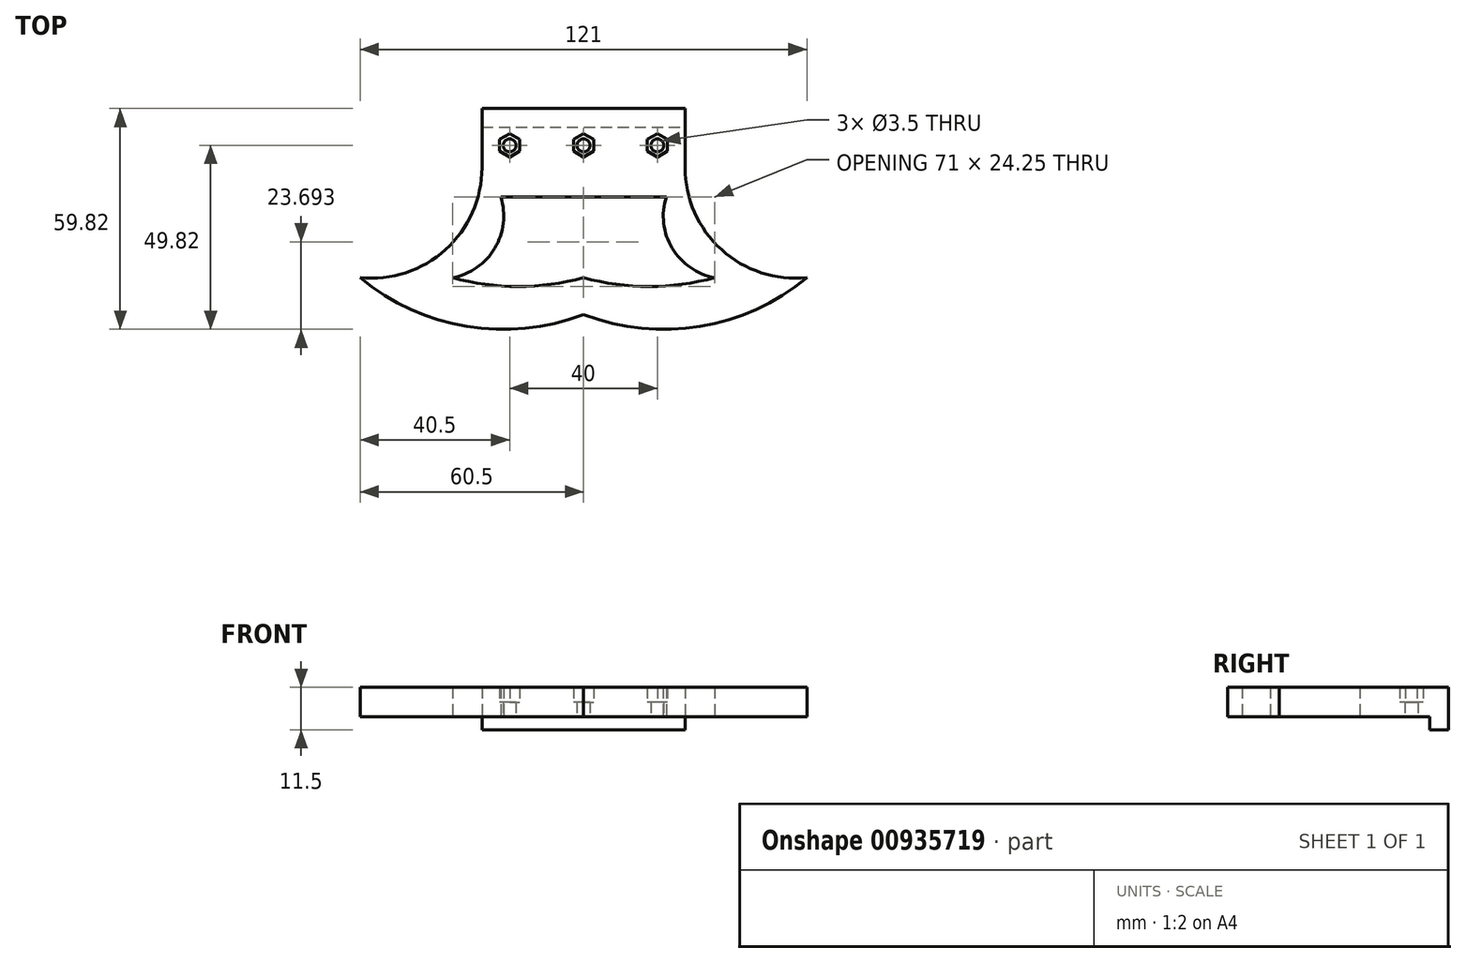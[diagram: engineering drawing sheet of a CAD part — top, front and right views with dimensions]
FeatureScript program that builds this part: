
annotation { "Feature Type Name" : "Feature", "Feature Type Description" : "" }
export const myFeature = defineFeature(function(context is Context, id is Id, definition is map)
    precondition{}
    {
        {
            var Q0;
            Q0=qCreatedBy(makeId("Top.planeOp"),FACE);
            var sketch = newSketch(context, id + "F0", { "sketchPlane" : qUnion([Q0])});
            skLineSegment(sketch, "E0.bottom", {"start": v(-27.5, -8) * mm, "end": v(27.5, -8) * mm});
            skLineSegment(sketch, "E0.top", {"start": v(-27.5, 8) * mm, "end": v(27.5, 8) * mm});
            skLineSegment(sketch, "E0.left", {"start": v(-27.5, -8) * mm, "end": v(-27.5, 8) * mm});
            skLineSegment(sketch, "E0.right", {"start": v(27.5, -8) * mm, "end": v(27.5, 8) * mm});
            skPoint(sketch, "E0.middle", {"position": v(0, 0) * mm});
            skLineSegment(sketch, "E1", {"start": v(-27.5, 3) * mm, "end": v(27.5, 3) * mm});
            skCircle(sketch, "E2.cCircle", {"center": v(0, -2) * mm, "radius": 2.75 * mm, "construction": true});
            skLineSegment(sketch, "E2.0", {"start": v(-2.75, -3.59) * mm, "end": v(-2.75, -0.41) * mm});
            skLineSegment(sketch, "E2.1", {"start": v(-2.75, -0.41) * mm, "end": v(0, 1.18) * mm});
            skLineSegment(sketch, "E2.2", {"start": v(0, 1.18) * mm, "end": v(2.75, -0.41) * mm});
            skLineSegment(sketch, "E2.3", {"start": v(2.75, -0.41) * mm, "end": v(2.75, -3.59) * mm});
            skLineSegment(sketch, "E2.4", {"start": v(2.75, -3.59) * mm, "end": v(0, -5.18) * mm});
            skLineSegment(sketch, "E2.5", {"start": v(0, -5.18) * mm, "end": v(-2.75, -3.59) * mm});
            skPoint(sketch, "E2.0.midPoint", {"position": v(-2.75, -2) * mm});
            skCircle(sketch, "E3", {"center": v(0, -2) * mm, "radius": 1.75 * mm});
            skCircle(sketch, "E4.cCircle", {"center": v(-20, -2) * mm, "radius": 2.75 * mm, "construction": true});
            skLineSegment(sketch, "E4.0", {"start": v(-17.25, -0.41) * mm, "end": v(-17.25, -3.59) * mm});
            skLineSegment(sketch, "E4.1", {"start": v(-17.25, -3.59) * mm, "end": v(-20, -5.18) * mm});
            skLineSegment(sketch, "E4.2", {"start": v(-20, -5.18) * mm, "end": v(-22.75, -3.59) * mm});
            skLineSegment(sketch, "E4.3", {"start": v(-22.75, -3.59) * mm, "end": v(-22.75, -0.41) * mm});
            skLineSegment(sketch, "E4.4", {"start": v(-22.75, -0.41) * mm, "end": v(-20, 1.18) * mm});
            skLineSegment(sketch, "E4.5", {"start": v(-20, 1.18) * mm, "end": v(-17.25, -0.41) * mm});
            skPoint(sketch, "E4.0.midPoint", {"position": v(-17.25, -2) * mm});
            skCircle(sketch, "E5", {"center": v(-20, -2) * mm, "radius": 1.75 * mm});
            skLineSegment(sketch, "E6.MirrorCS", {"start": v(17.25, -0.41) * mm, "end": v(17.25, -3.59) * mm});
            skLineSegment(sketch, "E7.MirrorCS", {"start": v(17.25, -3.59) * mm, "end": v(20, -5.18) * mm});
            skLineSegment(sketch, "E8.MirrorCS", {"start": v(20, -5.18) * mm, "end": v(22.75, -3.59) * mm});
            skLineSegment(sketch, "E9.MirrorCS", {"start": v(22.75, -3.59) * mm, "end": v(22.75, -0.41) * mm});
            skCircle(sketch, "E10.MirrorC", {"center": v(20, -2) * mm, "radius": 1.75 * mm});
            skCircle(sketch, "E11.MirrorC", {"center": v(20, -2) * mm, "radius": 2.75 * mm, "construction": true});
            skPoint(sketch, "E12.MirrorP", {"position": v(17.25, -2) * mm});
            skLineSegment(sketch, "E13.MirrorCS", {"start": v(20, 1.18) * mm, "end": v(17.25, -0.41) * mm});
            skLineSegment(sketch, "E14.MirrorCS", {"start": v(22.75, -0.41) * mm, "end": v(20, 1.18) * mm});
            skArc(sketch, "E15", {"start": v(27.5, -8) * mm, "mid": v(37.38, -30.25) * mm, "end": v(60.5, -37.85) * mm});
            skArc(sketch, "E16", {"start": v(0, -47.85) * mm, "mid": v(31.6, -51) * mm, "end": v(60.5, -37.85) * mm});
            skArc(sketch, "E17.MirrorCS", {"start": v(0, -47.85) * mm, "mid": v(-31.6, -51) * mm, "end": v(-60.5, -37.85) * mm});
            skArc(sketch, "E18.MirrorCS", {"start": v(-27.5, -8) * mm, "mid": v(-37.38, -30.25) * mm, "end": v(-60.5, -37.85) * mm});
            skLineSegment(sketch, "E19", {"start": v(-22.4, -16) * mm, "end": v(22.4, -16) * mm});
            skArc(sketch, "E20", {"start": v(22.4, -16) * mm, "mid": v(24.04, -29.87) * mm, "end": v(35.5, -37.85) * mm});
            skArc(sketch, "E21", {"start": v(0, -37.85) * mm, "mid": v(17.75, -40.25) * mm, "end": v(35.5, -37.85) * mm});
            skArc(sketch, "E22.MirrorCS", {"start": v(-22.4, -16) * mm, "mid": v(-24.04, -29.87) * mm, "end": v(-35.5, -37.85) * mm});
            skArc(sketch, "E23.MirrorCS", {"start": v(0, -37.85) * mm, "mid": v(-17.75, -40.25) * mm, "end": v(-35.5, -37.85) * mm});
            skSolve(sketch);
        }
        {
            var Q0;
            {var subQ0=sQuery(id+"F0.wireOp",EDGE,"E0.top");Q0=makeQuery(id+"F0.imprint","IMPRINT",FACE,{"disambiguationData":[TD([[makeQuery(id+"F0.imprint","IMPRINT",EDGE,{"derivedFrom":subQ0}),-1.0]])]});}
            var Q1;
            {var subQ0=sQuery(id+"F0.wireOp",EDGE,"E0.bottom");Q1=makeQuery(id+"F0.imprint","IMPRINT",FACE,{"disambiguationData":[TD([[makeQuery(id+"F0.imprint","IMPRINT",EDGE,{"derivedFrom":subQ0}),1.0]])]});}
            var Q2;
            Q2=makeQuery(id+"F0.imprint","IMPRINT",FACE,{"disambiguationData":[TD([[makeQuery(id+"F0.imprint","IMPRINT",EDGE,{"derivedFrom":sQuery(id+"F0.wireOp",EDGE,"E0.bottom")}),-1.0]])]});
            extrude(context, id + "F1", {"entities" : qUnion([Q0, Q1, Q2]), "depth" : 8 * mm, "offsetDistance" : 25 * mm});
        }
        {
            var Q0;
            Q0=makeQuery(id+"F0.imprint","IMPRINT",FACE,{"disambiguationData":[TD([[makeQuery(id+"F0.imprint","IMPRINT",EDGE,{"derivedFrom":sQuery(id+"F0.wireOp",EDGE,"E4.0")}),-1.0]])]});
            var Q1;
            Q1=makeQuery(id+"F0.imprint","IMPRINT",FACE,{"disambiguationData":[TD([[makeQuery(id+"F0.imprint","IMPRINT",EDGE,{"derivedFrom":sQuery(id+"F0.wireOp",EDGE,"E2.0")}),-1.0]])]});
            var Q2;
            Q2=makeQuery(id+"F0.imprint","IMPRINT",FACE,{"disambiguationData":[TD([[makeQuery(id+"F0.imprint","IMPRINT",EDGE,{"derivedFrom":sQuery(id+"F0.wireOp",EDGE,"E6.MirrorCS")}),1.0]])]});
            extrude(context, id + "F2", {"entities" : qUnion([Q0, Q1, Q2]), "operationType" : NewBodyOperationType.ADD, "depth" : 4 * mm, "offsetDistance" : 25 * mm});
        }
        {
            var Q0;
            {var subQ0=sQuery(id+"F0.wireOp",EDGE,"E0.top");Q0=makeQuery(id+"F0.imprint","IMPRINT",FACE,{"disambiguationData":[TD([[makeQuery(id+"F0.imprint","IMPRINT",EDGE,{"derivedFrom":subQ0}),-1.0]])]});}
            extrude(context, id + "F3", {"entities" : qUnion([Q0]), "operationType" : NewBodyOperationType.ADD, "oppositeDirection" : true, "depth" : 3.5 * mm, "offsetDistance" : 25 * mm});
        }
    });
